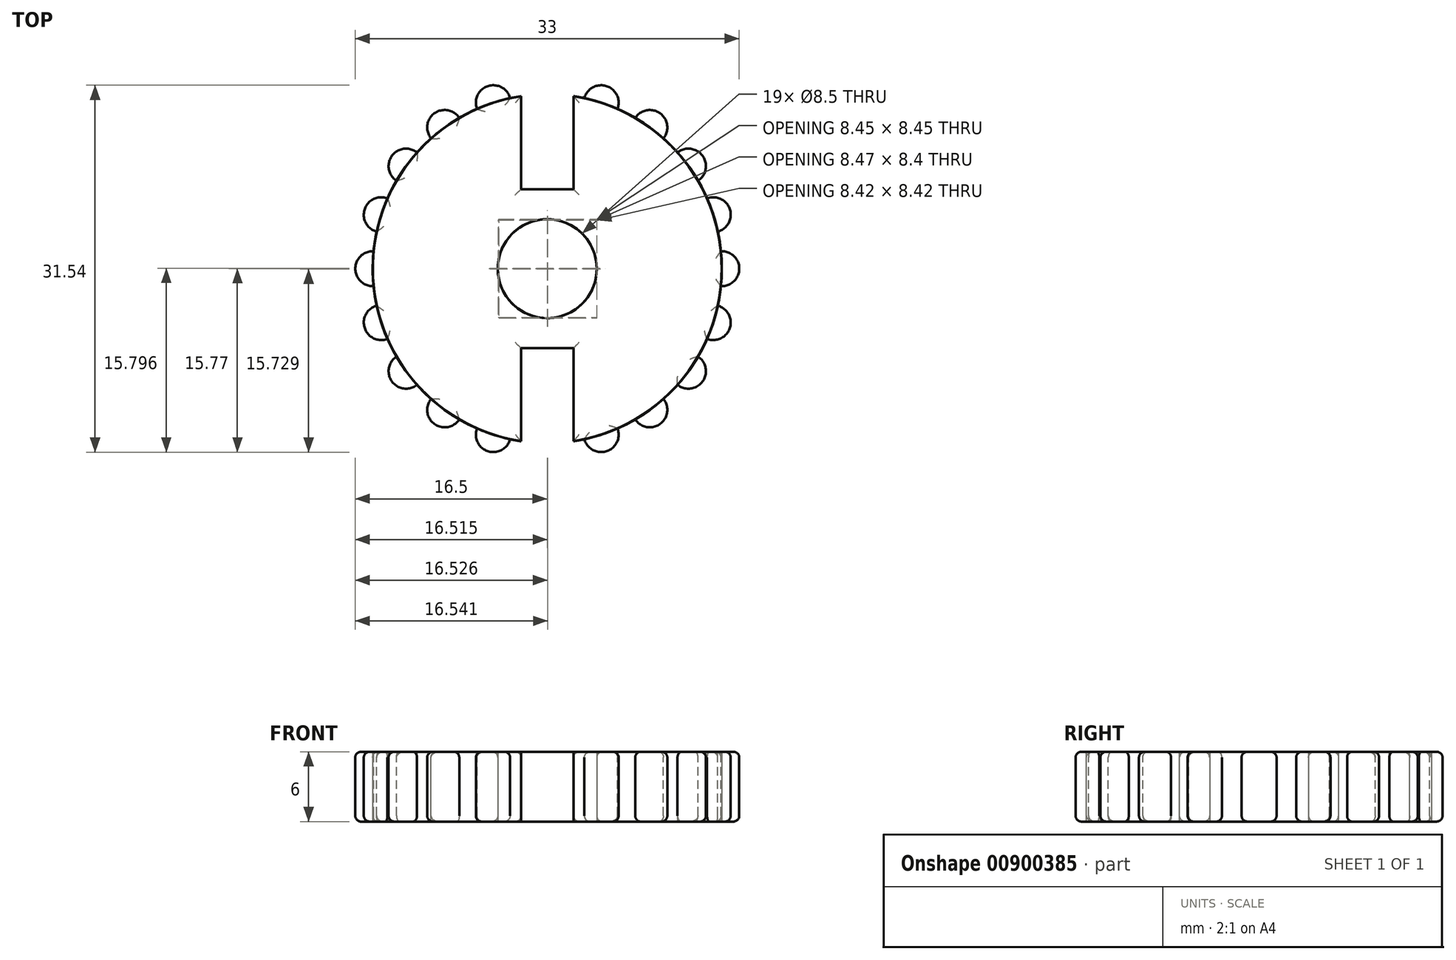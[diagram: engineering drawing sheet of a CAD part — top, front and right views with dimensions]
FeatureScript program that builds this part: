
annotation { "Feature Type Name" : "Feature", "Feature Type Description" : "" }
export const myFeature = defineFeature(function(context is Context, id is Id, definition is map)
    precondition{}
    {
        {
            var Q0;
            Q0=qCreatedBy(makeId("Top.planeOp"),FACE);
            var sketch = newSketch(context, id + "F0", { "sketchPlane" : qUnion([Q0])});
            skCircle(sketch, "E0", {"center": v(0, 0) * mm, "radius": 15 * mm});
            skCircle(sketch, "E1", {"center": v(0, 0) * mm, "radius": 4.25 * mm});
            skSolve(sketch);
        }
        {
            var Q0;
            Q0=makeQuery(id+"F0.imprint","IMPRINT",FACE,{"disambiguationData":[TD([[makeQuery(id+"F0.imprint","IMPRINT",EDGE,{"derivedFrom":sQuery(id+"F0.wireOp",EDGE,"E0")}),1.0]])]});
            extrude(context, id + "F1", {"entities" : qUnion([Q0]), "depth" : 6 * mm, "offsetDistance" : 25 * mm});
        }
        {
            var Q0;
            Q0=makeQuery(id+"F1.opExtrude","CAP_FACE",FACE,{"disambiguationData":[OSD([sQuery(id+"F0.wireOp",EDGE,"E0"),sQuery(id+"F0.wireOp",EDGE,"E1")])],"isStart":false});
            var sketch = newSketch(context, id + "F2", { "sketchPlane" : qUnion([Q0])});
            skCircle(sketch, "E2", {"center": v(0, 15) * mm, "radius": 1.5 * mm});
            skSolve(sketch);
        }
        {
            var Q0;
            {var subQ0=sQuery(id+"F2.wireOp",EDGE,"E2");var subQ1=makeQuery(id+"F1.opExtrude","CAP_EDGE",EDGE,{"disambiguationData":[OSD([sQuery(id+"F0.wireOp",EDGE,"E0")])],"isStart":false});var subQ2=makeQuery(id+"F2.imprint","INTERSECT",VERTEX,{"disambiguationData":[OD(0.0)],"derivedFrom":[subQ1,subQ0]});Q0=makeQuery(id+"F2.imprint","IMPRINT",FACE,{"disambiguationData":[TD([[makeQuery(id+"F2.imprint","IMPRINT",EDGE,{"disambiguationData":[TD([[subQ2,1.0]])],"derivedFrom":subQ0}),1.0]])]});}
            extrude(context, id + "F3", {"entities" : qUnion([Q0]), "operationType" : NewBodyOperationType.ADD, "oppositeDirection" : true, "depth" : 6 * mm, "offsetDistance" : 25 * mm});
        }
        {
            var Q0;
            Q0=qCreatedBy(makeId("Right.planeOp"),FACE);
            var sketch = newSketch(context, id + "F4", { "sketchPlane" : qUnion([Q0])});
            skLineSegment(sketch, "E3", {"start": v(0, 0) * mm, "end": v(0, 22.8) * mm});
            skSolve(sketch);
        }
        {
            var Q0;
            {var subQ0=sQuery(id+"F0.wireOp",EDGE,"E0");Q0=makeQuery(id+"F3.boolean.opBoolean","MERGE",FACE,{"derivedFrom":[makeQuery(id+"F1.opExtrude","CAP_FACE",FACE,{"disambiguationData":[OSD([subQ0,sQuery(id+"F0.wireOp",EDGE,"E1")])],"isStart":false}),makeQuery(id+"F3.opExtrude","CAP_FACE",FACE,{"disambiguationData":[OSD([subQ0,sQuery(id+"F2.wireOp",EDGE,"E2")])],"isStart":true})]});}
            var sketch = newSketch(context, id + "F5", { "sketchPlane" : qUnion([Q0])});
            skLineSegment(sketch, "E4", {"start": v(-2.25, 14.83) * mm, "end": v(-2.25, 6.83) * mm});
            skLineSegment(sketch, "E5", {"start": v(2.25, 14.83) * mm, "end": v(2.25, 6.83) * mm});
            skLineSegment(sketch, "E6", {"start": v(-2.25, 6.83) * mm, "end": v(2.25, 6.83) * mm});
            skLineSegment(sketch, "E7", {"start": v(0, 19.32) * mm, "end": v(0, -26.14) * mm, "construction": true});
            skLineSegment(sketch, "E8", {"start": v(-2.25, -14.83) * mm, "end": v(-2.25, -6.83) * mm});
            skLineSegment(sketch, "E9", {"start": v(2.25, -14.83) * mm, "end": v(2.25, -6.83) * mm});
            skLineSegment(sketch, "E10", {"start": v(2.25, -6.83) * mm, "end": v(-2.25, -6.83) * mm});
            skSolve(sketch);
        }
        {
            var Q0;
            Q0=makeQuery(id+"F1.opExtrude","SWEPT_BODY",BODY,{"disambiguationData":[OSD([sQuery(id+"F0.wireOp",EDGE,"E0"),sQuery(id+"F0.wireOp",EDGE,"E1")])]});
            var Q1;
            Q1=sQuery(id+"F4.wireOp",EDGE,"E3");
            circularPattern(context, id + "F6", {"entities" : qUnion([Q0]), "axis" : qUnion([Q1]), "angle" : 360 * degree, "instanceCount" : 20, "equalSpace" : true});
        }
        {
            var Q0;
            {var subQ0=sQuery(id+"F5.wireOp",EDGE,"E8");Q0=makeQuery(id+"F5.imprint","IMPRINT",FACE,{"disambiguationData":[TD([[makeQuery(id+"F5.imprint","IMPRINT",EDGE,{"derivedFrom":subQ0}),-1.0]])]});}
            var Q1;
            {var subQ2=sQuery(id+"F5.wireOp",EDGE,"E4");Q1=makeQuery(id+"F5.imprint","IMPRINT",FACE,{"disambiguationData":[TD([[makeQuery(id+"F5.imprint","IMPRINT",EDGE,{"derivedFrom":subQ2}),1.0]])]});}
            extrude(context, id + "F7", {"entities" : qUnion([Q0, Q1]), "operationType" : NewBodyOperationType.REMOVE, "oppositeDirection" : true, "depth" : 6 * mm, "offsetDistance" : 25 * mm});
        }
        {
            var Q0;
            Q0=makeQuery(id+"F7.boolean.opBoolean","SPLIT",BODY,{"disambiguationData":[OD(0.0)],"derivedFrom":makeQuery(id+"F6.opPattern","COPY",BODY,{"derivedFrom":makeQuery(id+"F1.opExtrude","SWEPT_BODY",BODY,{"disambiguationData":[OSD([sQuery(id+"F0.wireOp",EDGE,"E0"),sQuery(id+"F0.wireOp",EDGE,"E1")])]}),"instanceName":"10"})});
            deleteBodies(context, id + "F8", {"entities" : qUnion([Q0])});
        }
        {
            var Q0;
            Q0=makeQuery(id+"F6.opPattern","COPY",EDGE,{"derivedFrom":makeQuery(id+"F3.opExtrude","CAP_EDGE",EDGE,{"disambiguationData":[OSD([sQuery(id+"F2.wireOp",EDGE,"E2")])],"isStart":true}),"instanceName":"13"});
            var Q1;
            {var subQ1=sQuery(id+"F0.wireOp",EDGE,"E0");Q1=makeQuery(id+"F7.boolean.opBoolean","SPLIT",EDGE,{"disambiguationData":[TD([makeQuery(id+"F7.opExtrude","SWEPT_FACE",FACE,{"disambiguationData":[OSD([sQuery(id+"F5.wireOp",EDGE,"E9")])]})])],"derivedFrom":makeQuery(id+"F6.opPattern","COPY",EDGE,{"derivedFrom":makeQuery(id+"F1.opExtrude","CAP_EDGE",EDGE,{"disambiguationData":[OSD([subQ1])],"isStart":false}),"instanceName":"15"})});}
            var Q2;
            Q2=makeQuery(id+"F6.opPattern","COPY",EDGE,{"derivedFrom":makeQuery(id+"F3.opExtrude","CAP_EDGE",EDGE,{"disambiguationData":[OSD([sQuery(id+"F2.wireOp",EDGE,"E2")])],"isStart":true}),"instanceName":"12"});
            var Q3;
            Q3=makeQuery(id+"F6.opPattern","COPY",EDGE,{"derivedFrom":makeQuery(id+"F3.opExtrude","CAP_EDGE",EDGE,{"disambiguationData":[OSD([sQuery(id+"F2.wireOp",EDGE,"E2")])],"isStart":true}),"instanceName":"11"});
            var Q4;
            {var subQ0=sQuery(id+"F0.wireOp",EDGE,"E0");Q4=makeQuery(id+"F6.opPattern","COPY",FACE,{"derivedFrom":makeQuery(id+"F3.boolean.opBoolean","MERGE",FACE,{"derivedFrom":[makeQuery(id+"F1.opExtrude","CAP_FACE",FACE,{"disambiguationData":[OSD([subQ0,sQuery(id+"F0.wireOp",EDGE,"E1")])],"isStart":false}),makeQuery(id+"F3.opExtrude","CAP_FACE",FACE,{"disambiguationData":[OSD([subQ0,sQuery(id+"F2.wireOp",EDGE,"E2")])],"isStart":true})]}),"instanceName":"14"});}
            var Q5;
            Q5=makeQuery(id+"F6.opPattern","COPY",EDGE,{"derivedFrom":makeQuery(id+"F3.opExtrude","CAP_EDGE",EDGE,{"disambiguationData":[OSD([sQuery(id+"F2.wireOp",EDGE,"E2")])],"isStart":true}),"instanceName":"15"});
            var Q6;
            Q6=makeQuery(id+"F6.opPattern","COPY",EDGE,{"derivedFrom":makeQuery(id+"F3.opExtrude","CAP_EDGE",EDGE,{"disambiguationData":[OSD([sQuery(id+"F2.wireOp",EDGE,"E2")])],"isStart":true}),"instanceName":"16"});
            var Q7;
            Q7=makeQuery(id+"F6.opPattern","COPY",EDGE,{"derivedFrom":makeQuery(id+"F3.opExtrude","CAP_EDGE",EDGE,{"disambiguationData":[OSD([sQuery(id+"F2.wireOp",EDGE,"E2")])],"isStart":true}),"instanceName":"17"});
            var Q8;
            Q8=makeQuery(id+"F6.opPattern","COPY",EDGE,{"derivedFrom":makeQuery(id+"F3.opExtrude","CAP_EDGE",EDGE,{"disambiguationData":[OSD([sQuery(id+"F2.wireOp",EDGE,"E2")])],"isStart":true}),"instanceName":"18"});
            var Q9;
            Q9=makeQuery(id+"F6.opPattern","COPY",EDGE,{"derivedFrom":makeQuery(id+"F3.opExtrude","CAP_EDGE",EDGE,{"disambiguationData":[OSD([sQuery(id+"F2.wireOp",EDGE,"E2")])],"isStart":true}),"instanceName":"19"});
            var Q10;
            {var subQ0=sQuery(id+"F0.wireOp",EDGE,"E0");Q10=makeQuery(id+"F6.opPattern","COPY",FACE,{"derivedFrom":makeQuery(id+"F3.boolean.opBoolean","MERGE",FACE,{"derivedFrom":[makeQuery(id+"F1.opExtrude","CAP_FACE",FACE,{"disambiguationData":[OSD([subQ0,sQuery(id+"F0.wireOp",EDGE,"E1")])],"isStart":false}),makeQuery(id+"F3.opExtrude","CAP_FACE",FACE,{"disambiguationData":[OSD([subQ0,sQuery(id+"F2.wireOp",EDGE,"E2")])],"isStart":true})]}),"instanceName":"1"});}
            var Q11;
            {var subQ0=sQuery(id+"F0.wireOp",EDGE,"E0");Q11=makeQuery(id+"F6.opPattern","COPY",FACE,{"derivedFrom":makeQuery(id+"F3.boolean.opBoolean","MERGE",FACE,{"derivedFrom":[makeQuery(id+"F1.opExtrude","CAP_FACE",FACE,{"disambiguationData":[OSD([subQ0,sQuery(id+"F0.wireOp",EDGE,"E1")])],"isStart":false}),makeQuery(id+"F3.opExtrude","CAP_FACE",FACE,{"disambiguationData":[OSD([subQ0,sQuery(id+"F2.wireOp",EDGE,"E2")])],"isStart":true})]}),"instanceName":"2"});}
            var Q12;
            {var subQ0=sQuery(id+"F0.wireOp",EDGE,"E0");Q12=makeQuery(id+"F6.opPattern","COPY",FACE,{"derivedFrom":makeQuery(id+"F3.boolean.opBoolean","MERGE",FACE,{"derivedFrom":[makeQuery(id+"F1.opExtrude","CAP_FACE",FACE,{"disambiguationData":[OSD([subQ0,sQuery(id+"F0.wireOp",EDGE,"E1")])],"isStart":false}),makeQuery(id+"F3.opExtrude","CAP_FACE",FACE,{"disambiguationData":[OSD([subQ0,sQuery(id+"F2.wireOp",EDGE,"E2")])],"isStart":true})]}),"instanceName":"3"});}
            var Q13;
            Q13=makeQuery(id+"F6.opPattern","COPY",EDGE,{"derivedFrom":makeQuery(id+"F3.opExtrude","CAP_EDGE",EDGE,{"disambiguationData":[OSD([sQuery(id+"F2.wireOp",EDGE,"E2")])],"isStart":true}),"instanceName":"4"});
            var Q14;
            Q14=makeQuery(id+"F6.opPattern","COPY",EDGE,{"derivedFrom":makeQuery(id+"F3.opExtrude","CAP_EDGE",EDGE,{"disambiguationData":[OSD([sQuery(id+"F2.wireOp",EDGE,"E2")])],"isStart":true}),"instanceName":"5"});
            var Q15;
            {var subQ0=sQuery(id+"F0.wireOp",EDGE,"E0");Q15=makeQuery(id+"F6.opPattern","COPY",FACE,{"derivedFrom":makeQuery(id+"F3.boolean.opBoolean","MERGE",FACE,{"derivedFrom":[makeQuery(id+"F1.opExtrude","CAP_FACE",FACE,{"disambiguationData":[OSD([subQ0,sQuery(id+"F0.wireOp",EDGE,"E1")])],"isStart":false}),makeQuery(id+"F3.opExtrude","CAP_FACE",FACE,{"disambiguationData":[OSD([subQ0,sQuery(id+"F2.wireOp",EDGE,"E2")])],"isStart":true})]}),"instanceName":"6"});}
            var Q16;
            Q16=makeQuery(id+"F6.opPattern","COPY",EDGE,{"derivedFrom":makeQuery(id+"F3.opExtrude","CAP_EDGE",EDGE,{"disambiguationData":[OSD([sQuery(id+"F2.wireOp",EDGE,"E2")])],"isStart":true}),"instanceName":"7"});
            var Q17;
            Q17=makeQuery(id+"F6.opPattern","COPY",EDGE,{"derivedFrom":makeQuery(id+"F3.opExtrude","CAP_EDGE",EDGE,{"disambiguationData":[OSD([sQuery(id+"F2.wireOp",EDGE,"E2")])],"isStart":true}),"instanceName":"8"});
            var Q18;
            Q18=makeQuery(id+"F6.opPattern","COPY",EDGE,{"derivedFrom":makeQuery(id+"F3.opExtrude","CAP_EDGE",EDGE,{"disambiguationData":[OSD([sQuery(id+"F2.wireOp",EDGE,"E2")])],"isStart":true}),"instanceName":"9"});
            var Q19;
            {var subQ0=sQuery(id+"F0.wireOp",EDGE,"E0");Q19=makeQuery(id+"F3.boolean.opBoolean","MERGE",FACE,{"derivedFrom":[makeQuery(id+"F1.opExtrude","CAP_FACE",FACE,{"disambiguationData":[OSD([subQ0,sQuery(id+"F0.wireOp",EDGE,"E1")])],"isStart":false}),makeQuery(id+"F3.opExtrude","CAP_FACE",FACE,{"disambiguationData":[OSD([subQ0,sQuery(id+"F2.wireOp",EDGE,"E2")])],"isStart":true})]});}
            var Q20;
            Q20=makeQuery(id+"F6.opPattern","COPY",EDGE,{"derivedFrom":makeQuery(id+"F3.opExtrude","CAP_EDGE",EDGE,{"disambiguationData":[OSD([sQuery(id+"F2.wireOp",EDGE,"E2")])],"isStart":false}),"instanceName":"12"});
            var Q21;
            {var subQ0=sQuery(id+"F0.wireOp",EDGE,"E0");Q21=makeQuery(id+"F6.opPattern","COPY",FACE,{"derivedFrom":makeQuery(id+"F3.boolean.opBoolean","MERGE",FACE,{"derivedFrom":[makeQuery(id+"F1.opExtrude","CAP_FACE",FACE,{"disambiguationData":[OSD([subQ0,sQuery(id+"F0.wireOp",EDGE,"E1")])],"isStart":true}),makeQuery(id+"F3.opExtrude","CAP_FACE",FACE,{"disambiguationData":[OSD([subQ0,sQuery(id+"F2.wireOp",EDGE,"E2")])],"isStart":false})]}),"instanceName":"11"});}
            var Q22;
            {var subQ0=sQuery(id+"F0.wireOp",EDGE,"E0");Q22=makeQuery(id+"F6.opPattern","COPY",FACE,{"derivedFrom":makeQuery(id+"F3.boolean.opBoolean","MERGE",FACE,{"derivedFrom":[makeQuery(id+"F1.opExtrude","CAP_FACE",FACE,{"disambiguationData":[OSD([subQ0,sQuery(id+"F0.wireOp",EDGE,"E1")])],"isStart":true}),makeQuery(id+"F3.opExtrude","CAP_FACE",FACE,{"disambiguationData":[OSD([subQ0,sQuery(id+"F2.wireOp",EDGE,"E2")])],"isStart":false})]}),"instanceName":"13"});}
            var Q23;
            Q23=makeQuery(id+"F6.opPattern","COPY",EDGE,{"derivedFrom":makeQuery(id+"F3.opExtrude","CAP_EDGE",EDGE,{"disambiguationData":[OSD([sQuery(id+"F2.wireOp",EDGE,"E2")])],"isStart":false}),"instanceName":"14"});
            var Q24;
            {var subQ0=sQuery(id+"F0.wireOp",EDGE,"E0");Q24=makeQuery(id+"F6.opPattern","COPY",FACE,{"derivedFrom":makeQuery(id+"F3.boolean.opBoolean","MERGE",FACE,{"derivedFrom":[makeQuery(id+"F1.opExtrude","CAP_FACE",FACE,{"disambiguationData":[OSD([subQ0,sQuery(id+"F0.wireOp",EDGE,"E1")])],"isStart":true}),makeQuery(id+"F3.opExtrude","CAP_FACE",FACE,{"disambiguationData":[OSD([subQ0,sQuery(id+"F2.wireOp",EDGE,"E2")])],"isStart":false})]}),"instanceName":"15"});}
            var Q25;
            Q25=makeQuery(id+"F6.opPattern","COPY",EDGE,{"derivedFrom":makeQuery(id+"F3.opExtrude","CAP_EDGE",EDGE,{"disambiguationData":[OSD([sQuery(id+"F2.wireOp",EDGE,"E2")])],"isStart":false}),"instanceName":"16"});
            var Q26;
            Q26=makeQuery(id+"F6.opPattern","COPY",EDGE,{"derivedFrom":makeQuery(id+"F3.opExtrude","CAP_EDGE",EDGE,{"disambiguationData":[OSD([sQuery(id+"F2.wireOp",EDGE,"E2")])],"isStart":false}),"instanceName":"17"});
            var Q27;
            Q27=makeQuery(id+"F6.opPattern","COPY",EDGE,{"derivedFrom":makeQuery(id+"F3.opExtrude","CAP_EDGE",EDGE,{"disambiguationData":[OSD([sQuery(id+"F2.wireOp",EDGE,"E2")])],"isStart":false}),"instanceName":"18"});
            var Q28;
            Q28=makeQuery(id+"F6.opPattern","COPY",EDGE,{"derivedFrom":makeQuery(id+"F3.opExtrude","CAP_EDGE",EDGE,{"disambiguationData":[OSD([sQuery(id+"F2.wireOp",EDGE,"E2")])],"isStart":false}),"instanceName":"19"});
            var Q29;
            Q29=makeQuery(id+"F6.opPattern","COPY",EDGE,{"derivedFrom":makeQuery(id+"F3.opExtrude","CAP_EDGE",EDGE,{"disambiguationData":[OSD([sQuery(id+"F2.wireOp",EDGE,"E2")])],"isStart":false}),"instanceName":"1"});
            var Q30;
            Q30=makeQuery(id+"F6.opPattern","COPY",EDGE,{"derivedFrom":makeQuery(id+"F3.opExtrude","CAP_EDGE",EDGE,{"disambiguationData":[OSD([sQuery(id+"F2.wireOp",EDGE,"E2")])],"isStart":false}),"instanceName":"3"});
            var Q31;
            {var subQ0=sQuery(id+"F0.wireOp",EDGE,"E0");Q31=makeQuery(id+"F6.opPattern","COPY",FACE,{"derivedFrom":makeQuery(id+"F3.boolean.opBoolean","MERGE",FACE,{"derivedFrom":[makeQuery(id+"F1.opExtrude","CAP_FACE",FACE,{"disambiguationData":[OSD([subQ0,sQuery(id+"F0.wireOp",EDGE,"E1")])],"isStart":true}),makeQuery(id+"F3.opExtrude","CAP_FACE",FACE,{"disambiguationData":[OSD([subQ0,sQuery(id+"F2.wireOp",EDGE,"E2")])],"isStart":false})]}),"instanceName":"4"});}
            var Q32;
            Q32=makeQuery(id+"F6.opPattern","COPY",EDGE,{"derivedFrom":makeQuery(id+"F3.opExtrude","CAP_EDGE",EDGE,{"disambiguationData":[OSD([sQuery(id+"F2.wireOp",EDGE,"E2")])],"isStart":false}),"instanceName":"5"});
            var Q33;
            Q33=makeQuery(id+"F6.opPattern","COPY",EDGE,{"derivedFrom":makeQuery(id+"F3.opExtrude","CAP_EDGE",EDGE,{"disambiguationData":[OSD([sQuery(id+"F2.wireOp",EDGE,"E2")])],"isStart":false}),"instanceName":"6"});
            var Q34;
            Q34=makeQuery(id+"F6.opPattern","COPY",EDGE,{"derivedFrom":makeQuery(id+"F3.opExtrude","CAP_EDGE",EDGE,{"disambiguationData":[OSD([sQuery(id+"F2.wireOp",EDGE,"E2")])],"isStart":false}),"instanceName":"7"});
            var Q35;
            Q35=makeQuery(id+"F6.opPattern","COPY",EDGE,{"derivedFrom":makeQuery(id+"F3.opExtrude","CAP_EDGE",EDGE,{"disambiguationData":[OSD([sQuery(id+"F2.wireOp",EDGE,"E2")])],"isStart":false}),"instanceName":"8"});
            var Q36;
            Q36=makeQuery(id+"F6.opPattern","COPY",EDGE,{"derivedFrom":makeQuery(id+"F3.opExtrude","CAP_EDGE",EDGE,{"disambiguationData":[OSD([sQuery(id+"F2.wireOp",EDGE,"E2")])],"isStart":false}),"instanceName":"9"});
            var Q37;
            {var subQ0=sQuery(id+"F0.wireOp",EDGE,"E0");Q37=makeQuery(id+"F6.opPattern","COPY",FACE,{"derivedFrom":makeQuery(id+"F3.boolean.opBoolean","MERGE",FACE,{"derivedFrom":[makeQuery(id+"F1.opExtrude","CAP_FACE",FACE,{"disambiguationData":[OSD([subQ0,sQuery(id+"F0.wireOp",EDGE,"E1")])],"isStart":true}),makeQuery(id+"F3.opExtrude","CAP_FACE",FACE,{"disambiguationData":[OSD([subQ0,sQuery(id+"F2.wireOp",EDGE,"E2")])],"isStart":false})]}),"instanceName":"8"});}
            fillet(context, id + "F9", {"entities" : qUnion([Q0, Q1, Q2, Q3, Q4, Q5, Q6, Q7, Q8, Q9, Q10, Q11, Q12, Q13, Q14, Q15, Q16, Q17, Q18, Q19, Q20, Q21, Q22, Q23, Q24, Q25, Q26, Q27, Q28, Q29, Q30, Q31, Q32, Q33, Q34, Q35, Q36, Q37]), "radius" : .5 * mm, "tangentPropagation" : true, "allowEdgeOverflow" : false});
        }
    });
